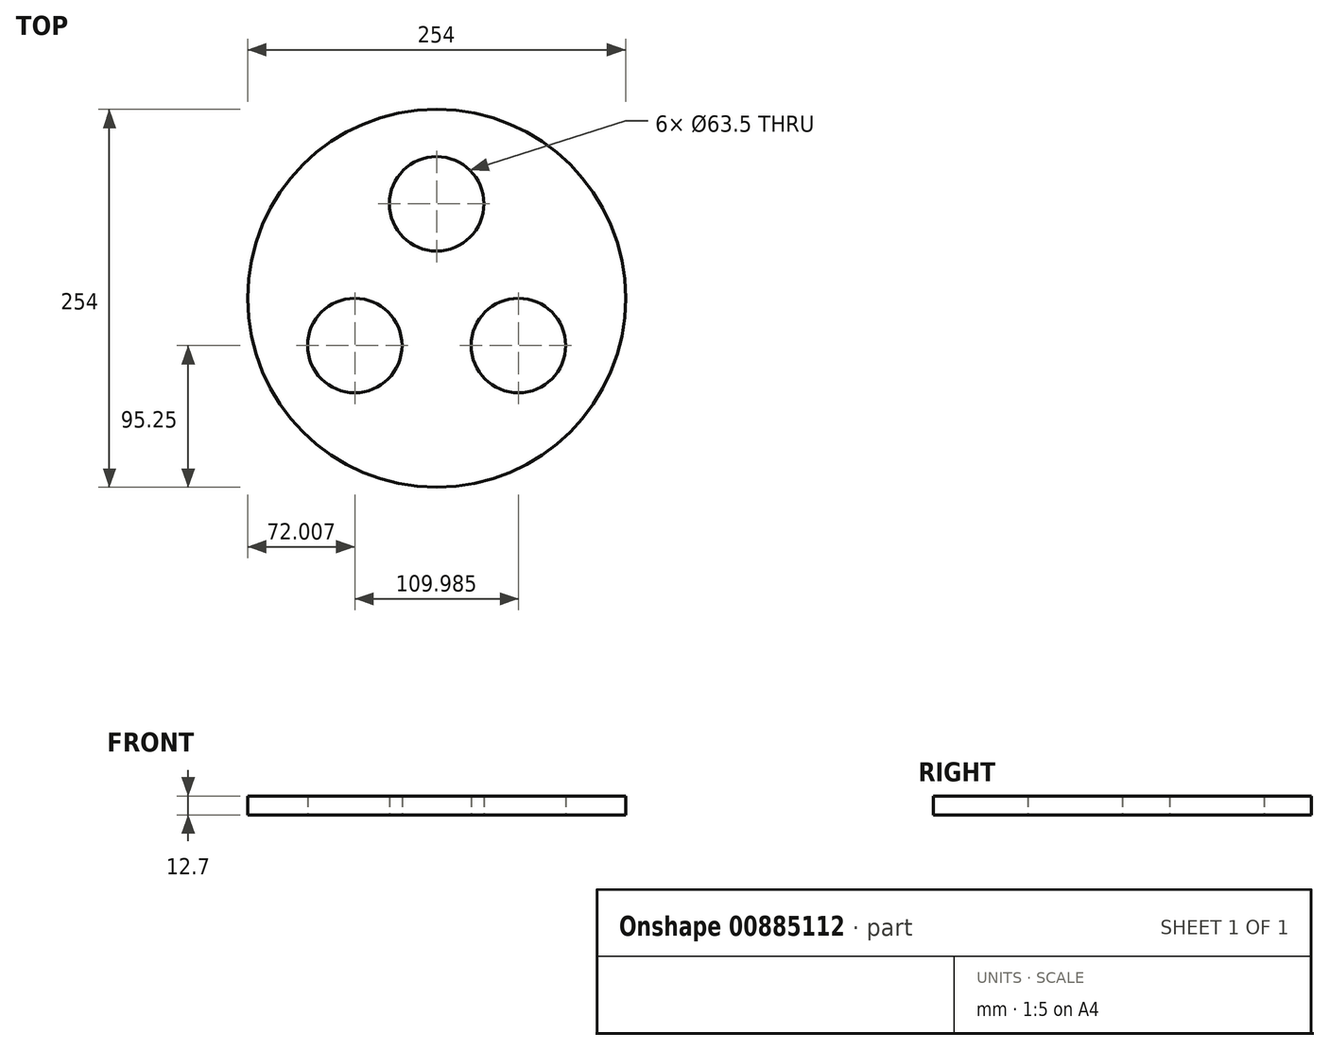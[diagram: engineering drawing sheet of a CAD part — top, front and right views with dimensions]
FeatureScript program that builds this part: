
annotation { "Feature Type Name" : "Feature", "Feature Type Description" : "" }
export const myFeature = defineFeature(function(context is Context, id is Id, definition is map)
    precondition{}
    {
        {
            var Q0;
            Q0=qCreatedBy(makeId("Top.planeOp"),FACE);
            var sketch = newSketch(context, id + "F0", { "sketchPlane" : qUnion([Q0])});
            skCircle(sketch, "E0", {"center": v(0, 0) * mm, "radius": 114.3 * mm, "construction": true});
            skCircle(sketch, "E1", {"center": v(0, 63.5) * mm, "radius": 50.8 * mm, "construction": true});
            skCircle(sketch, "E2", {"center": v(0, 63.5) * mm, "radius": 31.75 * mm});
            skCircle(sketch, "E3.1.0", {"center": v(-55, -31.75) * mm, "radius": 31.75 * mm});
            skCircle(sketch, "E3.1.1", {"center": v(-55, -31.75) * mm, "radius": 50.8 * mm, "construction": true});
            skCircle(sketch, "E3.2.0", {"center": v(55, -31.75) * mm, "radius": 31.75 * mm});
            skCircle(sketch, "E3.2.1", {"center": v(55, -31.75) * mm, "radius": 50.8 * mm, "construction": true});
            skCircle(sketch, "E4", {"center": v(0, 0) * mm, "radius": 127 * mm});
            skCircle(sketch, "E5", {"center": v(0, 0) * mm, "radius": 12.7 * mm, "construction": true});
            skSolve(sketch);
        }
        {
            var Q0;
            Q0=makeQuery(id+"F0.imprint","IMPRINT",FACE,{"disambiguationData":[TD([[makeQuery(id+"F0.imprint","IMPRINT",EDGE,{"derivedFrom":sQuery(id+"F0.wireOp",EDGE,"E2")}),-1.0]])]});
            extrude(context, id + "F1", {"entities" : qUnion([Q0]), "depth" : 12.7 * mm, "offsetDistance" : 25.4 * mm});
        }
    });
